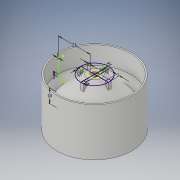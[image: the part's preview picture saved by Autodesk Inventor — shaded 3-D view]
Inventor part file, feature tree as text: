
AUTODESK INVENTOR PART (.ipt)
format: ipt  version: 2019 (Build 230136000, 136)  size: 242,688 bytes
history: native  units: in
note: dims shown in document units (in); Inventor stores cm internally (conversion verified against a paired STEP export)
features: revolve x4, extrude x4, sketch x3
ambient origin geometry x8: Origin, YZ Plane, XZ Plane, XY Plane, X Axis, Y Axis, Z Axis, Center Point
bodies: Solid1 (feature_tree)
feature tree (11):
  sketch  "Sketch1"  dims[d20=0.0787in d21=0.0787in]
  revolve  "Revolution4"  [1 undecoded]
  sketch  "Sketch2"  dims[d26=90.0deg d29=0.7874in]
  revolve  "Revolution10"  [1 undecoded]
  extrude  "Extrusion5"  Depth=0.0787in
  extrude  "Extrusion6"  Depth=0.3937in
  extrude  "Extrusion7"  Depth=0.0787in
  extrude  "Extrusion8"  Depth=0.0787in
  revolve  "Revolution11"  [1 undecoded]
  sketch  "Sketch3"  dims[d34=0.0787in d35=0.0787in d50=0.0394in d54=0.0787in d56=0.0787in d57=0.0787in d58=90.0deg d59=0.5512in d60=0.0in d61=0.5512in d62=0.0in d63=0.5512in d64=0.0in d65=0.5512in d66=0.0in d67=0.9055in d69=0.0787in d70=90.0deg d71=0.3937in d72=90.0deg]
  revolve  "Revolution12"  Angle=90.0deg
note: 3 required parameter values undecoded (feature->parameter linkage not recoverable at this tier; creation-order binding heuristic only, values carry confidence <= 0.55)
